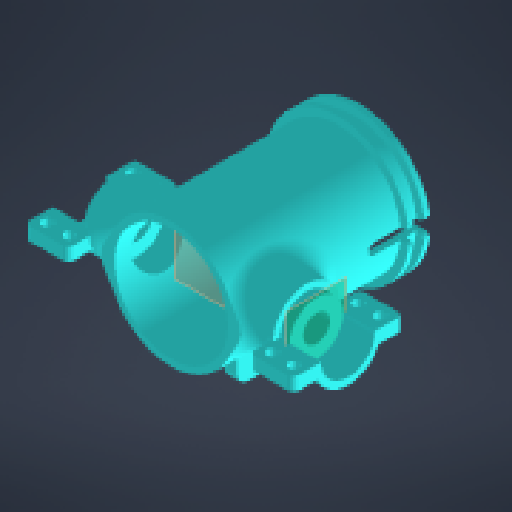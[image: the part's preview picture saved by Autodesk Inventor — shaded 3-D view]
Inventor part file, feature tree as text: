
AUTODESK INVENTOR PART (.ipt)
format: ipt  version: 2024 (Build 280153000, 153)  size: 508,928 bytes
history: native  units: mm
features: sketch x12, extrude x10, other x8, fillet x6, mirror x3, revolve x2
ambient origin geometry x8: Origin, YZ Plane, XZ Plane, XY Plane, X Axis, Y Axis, Z Axis, Center Point
bodies: Body1 (feature_tree)
feature tree (41):
  other  "Твердое тело1"
  extrude  "Выдавливание1"  Depth=70.0mm TaperAngle=0.0deg
  other  "РабПлоскость2"
  revolve  "Вращение1"
  fillet  "Сопряжение1"  Radius=47.0mm
  extrude  "Выдавливание2"  [1 undecoded]
  extrude  "Выдавливание3"  Depth=100.0mm
  extrude  "Выдавливание4"  Depth=25.0mm
  fillet  "Сопряжение2"  [1 undecoded]
  extrude  "Выдавливание5"  Depth=10.0mm
  revolve  "Вращение2"
  fillet  "Сопряжение3"  Radius=20.0mm
  extrude  "Выдавливание6"  TaperAngle=0.0deg  [1 undecoded]
  fillet  "Сопряжение4"  Radius=12.0mm
  fillet  "Сопряжение5"  Radius=5.0mm
  other  "РабПлоскость4"
  extrude  "Выдавливание8"  Depth=7.5mm
  extrude  "Выдавливание11"  Depth=40.0mm TaperAngle=0.0deg
  extrude  "Выдавливание12"  Depth=3.0mm
  fillet  "Сопряжение6"  Radius=5.0mm
  mirror  "Зеркальное отражение5"
  mirror  "Зеркальное отражение6"
  other  "РабПлоскость6"
  extrude  "Выдавливание13"  Depth=8.0mm
  mirror  "Зеркальное отражение7"
  sketch  "Эскиз1"
  sketch  "Эскиз3"
  sketch  "Эскиз4"
  sketch  "Эскиз5"
  sketch  "Эскиз6"
  sketch  "Эскиз7"
  sketch  "Эскиз8"
  sketch  "Эскиз9"
  sketch  "Эскиз11"
  sketch  "Эскиз14"
  sketch  "Эскиз15"
  sketch  "Эскиз16"
  parser-record x1  (decoder bookkeeping rows leaked as tree rows — omitted from the tree; the rows remain in map.json)
  other  "default_motor_asembly.iam"
  other  "bushing_assembly:1"
  other  "bushing:1"
note: 3 required parameter values undecoded (feature->parameter linkage not recoverable at this tier; creation-order binding heuristic only, values carry confidence <= 0.55)
note: 1 file-system path scrubbed to <path> (originals preserved in map.json)
